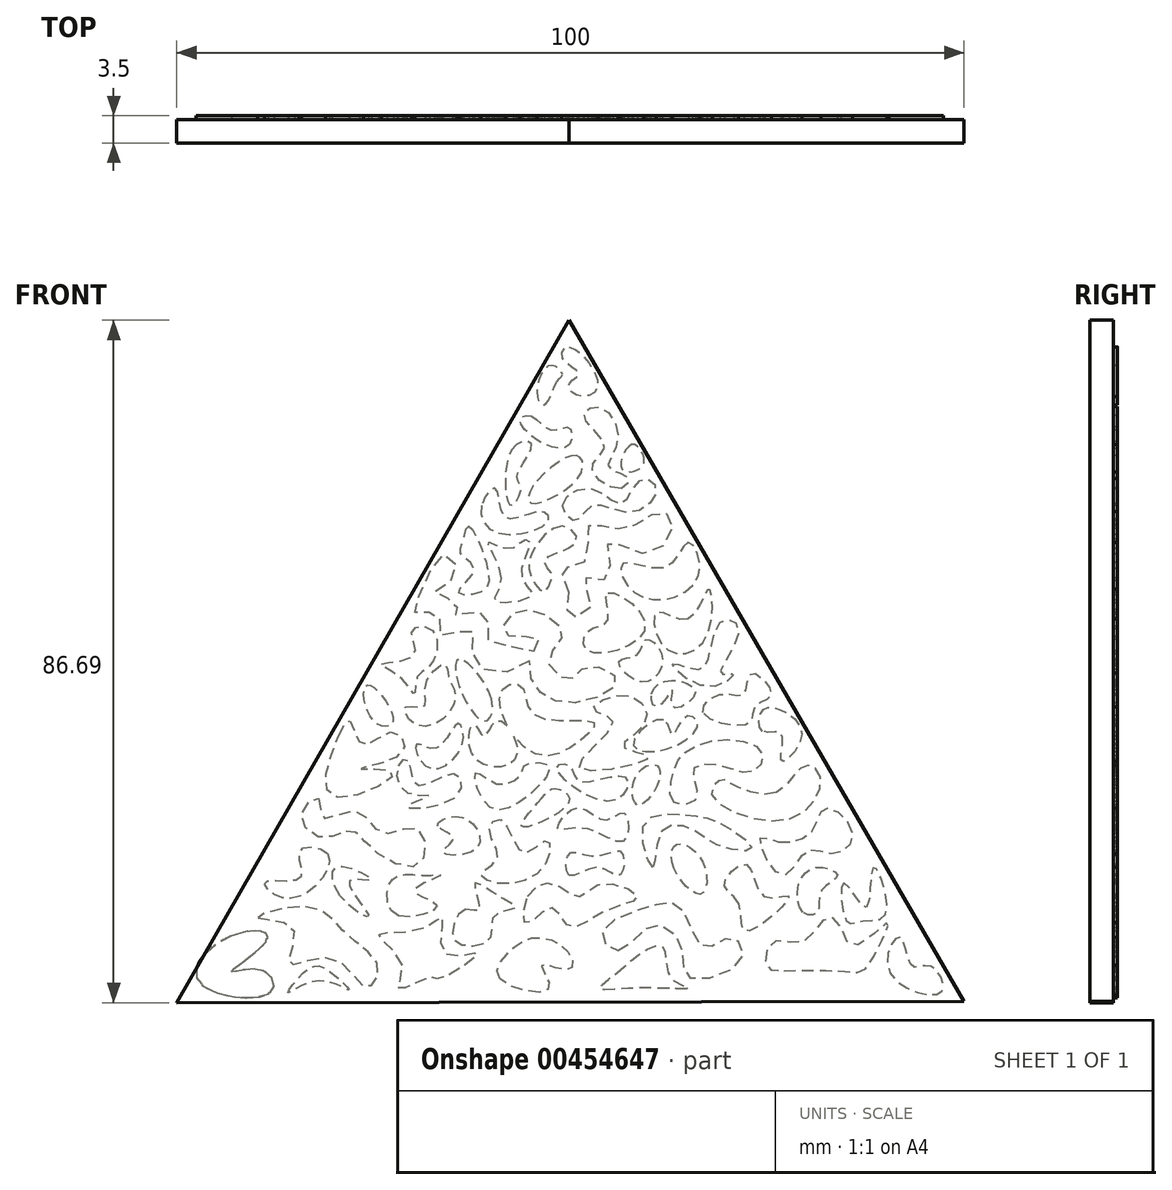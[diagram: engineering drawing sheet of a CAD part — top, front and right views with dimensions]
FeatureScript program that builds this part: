
annotation { "Feature Type Name" : "Feature", "Feature Type Description" : "" }
export const myFeature = defineFeature(function(context is Context, id is Id, definition is map)
    precondition{}
    {
        {
            var Q0;
            Q0=qCreatedBy(makeId("Front.planeOp"),FACE);
            var sketch = newSketch(context, id + "F0", { "sketchPlane" : qUnion([Q0])});
            skCircle(sketch, "E0.cCircle", {"center": v(0, 0) * mm, "radius": 28.87 * mm, "construction": true});
            skLineSegment(sketch, "E0.0", {"start": v(-49.85, 0) * mm, "end": v(0, 86.69) * mm});
            skLineSegment(sketch, "E0.1", {"start": v(0, 86.69) * mm, "end": v(50.15, 0.17) * mm});
            skLineSegment(sketch, "E0.2", {"start": v(50.15, 0.17) * mm, "end": v(-49.85, 0) * mm});
            skPoint(sketch, "E0.0.midPoint", {"position": v(25.08, -14.3) * mm});
            skSolve(sketch);
        }
        {
            var Q0;
            Q0 = qSketchRegion(id + "F0", true);
            extrude(context, id + "F1", {"entities" : qUnion([Q0]), "depth" : 3 * mm});
        }
        {
            var Q0;
            Q0=qCreatedBy(makeId("Front.planeOp"),FACE);
            var sketch = newSketch(context, id + "F2", { "sketchPlane" : qUnion([Q0])});
            skFitSpline(sketch, "E1", {"points": [v(0, 83.29) * mm, v(3.64, 78.3) * mm, v(1.1, 77.14) * mm, v(0, 78.6) * mm, v(1.2, 79.87) * mm, v(-0.86, 81.92) * mm, v(0, 83.29) * mm]});
            skFitSpline(sketch, "E2", {"points": [v(-1.54, 78.9) * mm, v(-0.86, 79.87) * mm, v(-2.42, 80.95) * mm, v(-4.08, 77.14) * mm, v(-3.1, 75.96) * mm, v(-1.54, 78.9) * mm]});
            skFitSpline(sketch, "E3", {"points": [v(-4.76, 74.5) * mm, v(-2.22, 72.74) * mm, v(0, 73.03) * mm, v(0, 70.88) * mm, v(-3.6, 71.18) * mm, v(-6.23, 74.1) * mm, v(-4.76, 74.5) * mm]});
            skFitSpline(sketch, "E4", {"points": [v(6.66, 65.32) * mm, v(2.85, 67.86) * mm, v(4.52, 70.69) * mm, v(1.88, 74.5) * mm, v(3.83, 75.67) * mm, v(6.18, 71.47) * mm, v(5, 67.95) * mm, v(7.35, 66.78) * mm, v(6.66, 65.32) * mm]});
            skFitSpline(sketch, "E5", {"points": [v(0.9, 69.52) * mm, v(-4.76, 65.32) * mm, v(-4.76, 63.46) * mm, v(1.39, 67.07) * mm, v(0.9, 69.52) * mm]});
            skFitSpline(sketch, "E6", {"points": [v(-11.11, 63.17) * mm, v(-9.06, 59.65) * mm, v(-2.62, 61.21) * mm, v(-3.6, 62.39) * mm, v(-8.09, 61.6) * mm, v(-9.36, 65.32) * mm, v(-11.11, 63.17) * mm]});
            skFitSpline(sketch, "E7", {"points": [v(-6.72, 70.88) * mm, v(-8.09, 65.32) * mm, v(-7.3, 63.17) * mm, v(-6.13, 65.32) * mm, v(-6.62, 66.98) * mm, v(-4.76, 70.88) * mm, v(-6.72, 70.88) * mm]});
            skFitSpline(sketch, "E8", {"points": [v(7.93, 70.88) * mm, v(6.66, 67.86) * mm, v(9, 67.86) * mm, v(9.4, 69.52) * mm, v(7.93, 70.88) * mm]});
            skFitSpline(sketch, "E9", {"points": [v(-0.86, 63.17) * mm, v(2.85, 65.32) * mm, v(6.66, 63.46) * mm, v(9.2, 66.49) * mm, v(11.06, 65.32) * mm, v(7.93, 62.29) * mm, v(2.85, 63.17) * mm, v(0.9, 61.21) * mm, v(-0.86, 63.17) * mm]});
            skFitSpline(sketch, "E10", {"points": [v(-0.86, 60.53) * mm, v(-4.76, 57.01) * mm, v(-4.76, 53.98) * mm, v(-3.1, 52.23) * mm, v(-2.22, 53.89) * mm, v(-2.22, 54.57) * mm, v(-3.1, 56.23) * mm, v(0.9, 58.48) * mm, v(-0.86, 60.53) * mm]});
            skFitSpline(sketch, "E11", {"points": [v(-12.77, 60.53) * mm, v(-10.33, 55.06) * mm, v(-11.11, 52.23) * mm, v(-14.04, 52.13) * mm, v(-12.1, 54.96) * mm, v(-13.75, 57.01) * mm, v(-13.46, 58.77) * mm, v(-12.77, 60.53) * mm]});
            skFitSpline(sketch, "E12", {"points": [v(-8.57, 53.89) * mm, v(-10.33, 58.48) * mm, v(-7.6, 57.7) * mm, v(-5.55, 58.87) * mm, v(-5.06, 58.28) * mm, v(-6.03, 53.98) * mm, v(-4.76, 51.74) * mm, v(-9.36, 50.96) * mm, v(-8.57, 53.89) * mm]});
            skFitSpline(sketch, "E13", {"points": [v(0, 52.13) * mm, v(-0.86, 55.06) * mm, v(2.13, 56.23) * mm, v(2.46, 60.53) * mm, v(4.43, 60.53) * mm, v(8.04, 60.53) * mm, v(11.66, 62.39) * mm, v(13.14, 60.53) * mm, v(9.69, 57.01) * mm, v(4.92, 58.44) * mm, v(4.92, 53.89) * mm, v(1.8, 53.89) * mm, v(2.79, 50.39) * mm, v(0, 49.08) * mm, v(0, 52.13) * mm]});
            skFitSpline(sketch, "E14", {"points": [v(15.1, 58.44) * mm, v(12.31, 55.32) * mm, v(6.9, 55.81) * mm, v(7.39, 53.02) * mm, v(12.15, 51.21) * mm, v(16.59, 54.83) * mm, v(15.1, 58.44) * mm]});
            skFitSpline(sketch, "E15", {"points": [v(4.92, 52.03) * mm, v(9.69, 47.76) * mm, v(2.46, 44.64) * mm, v(2.46, 47.27) * mm, v(4.92, 48.58) * mm, v(4.92, 52.03) * mm]});
            skFitSpline(sketch, "E16", {"points": [v(-7.24, 49.4) * mm, v(-3.3, 49.4) * mm, v(-0.86, 46.61) * mm, v(-2.64, 43.49) * mm, v(0, 41.03) * mm, v(2.13, 42.67) * mm, v(6.07, 41.03) * mm, v(1.64, 38.23) * mm, v(-3.62, 39.38) * mm, v(-4.94, 43.65) * mm, v(-3.95, 46.28) * mm, v(-8.06, 46.78) * mm, v(-7.24, 49.4) * mm]});
            skFitSpline(sketch, "E17", {"points": [v(-14.46, 54.17) * mm, v(-17.1, 52.03) * mm, v(-14.14, 50.72) * mm, v(-14.8, 49.4) * mm, v(-10.52, 49.4) * mm, v(-10.36, 46.12) * mm, v(-4.48, 44.68) * mm, v(-7.24, 42.18) * mm, v(-12.16, 43.65) * mm, v(-12.5, 47.43) * mm, v(-16.27, 46.61) * mm, v(-16.6, 49.4) * mm, v(-19.4, 49.4) * mm, v(-18.9, 52.03) * mm, v(-15.61, 57.01) * mm, v(-14.46, 54.17) * mm]});
            skFitSpline(sketch, "E18", {"points": [v(15.1, 48.75) * mm, v(11.16, 49.57) * mm, v(12.15, 45.13) * mm, v(17.24, 46.12) * mm, v(17.74, 52.53) * mm, v(15.1, 48.75) * mm]});
            skFitSpline(sketch, "E19", {"points": [v(-9.86, 38.56) * mm, v(-13.97, 43.65) * mm, v(-13.97, 40.2) * mm, v(-10.69, 35.77) * mm, v(-9.86, 38.56) * mm]});
            skFitSpline(sketch, "E20", {"points": [v(-8.71, 39.38) * mm, v(-6.09, 40.2) * mm, v(-4.48, 36.59) * mm, v(3.11, 35.6) * mm, v(1.8, 33.63) * mm, v(-4.48, 31.66) * mm, v(-8.71, 39.38) * mm]});
            skFitSpline(sketch, "E21", {"points": [v(1.3, 29.85) * mm, v(5.58, 35.6) * mm, v(3.11, 37.25) * mm, v(7.39, 39.05) * mm, v(9.69, 35.6) * mm, v(6.9, 32.48) * mm, v(10.18, 31.17) * mm, v(1.3, 29.85) * mm]});
            skFitSpline(sketch, "E22", {"points": [v(-25.64, 40.37) * mm, v(-22.35, 35.77) * mm, v(-24.81, 35.77) * mm, v(-25.64, 40.37) * mm]});
            skFitSpline(sketch, "E23", {"points": [v(-19.4, 32.81) * mm, v(-17.91, 29.85) * mm, v(-13.64, 32.65) * mm, v(-14.14, 35.44) * mm, v(-16.93, 32.32) * mm, v(-19.4, 32.81) * mm]});
            skFitSpline(sketch, "E24", {"points": [v(-12.1, 35.37) * mm, v(-10.83, 33.8) * mm, v(-9.07, 35.86) * mm, v(-6.72, 31.17) * mm, v(-12.1, 31.17) * mm, v(-12.1, 35.37) * mm]});
            skFitSpline(sketch, "E25", {"points": [v(6.33, 43.33) * mm, v(8.71, 44.24) * mm, v(9.7, 46.12) * mm, v(11.83, 43.9) * mm, v(9.37, 40.7) * mm, v(6.33, 43.33) * mm]});
            skFitSpline(sketch, "E26", {"points": [v(13.15, 43) * mm, v(16.02, 42.35) * mm, v(17.58, 43.41) * mm, v(19.47, 48.59) * mm, v(21.53, 47.27) * mm, v(19.23, 41.77) * mm, v(20.87, 41.85) * mm, v(17.83, 40.13) * mm, v(13.15, 43) * mm]});
            skFitSpline(sketch, "E27", {"points": [v(10.44, 39.22) * mm, v(13.15, 40.95) * mm, v(16.02, 39.22) * mm, v(13.15, 37.58) * mm, v(13.15, 39.72) * mm, v(11.18, 37.58) * mm, v(10.44, 39.22) * mm]});
            skFitSpline(sketch, "E28", {"points": [v(12, 35.94) * mm, v(8.14, 32.98) * mm, v(11.92, 32.08) * mm, v(16.35, 35.45) * mm, v(14.8, 36.35) * mm, v(13.15, 33.97) * mm, v(12, 35.94) * mm]});
            skFitSpline(sketch, "E29", {"points": [v(17, 36.84) * mm, v(19.55, 39.22) * mm, v(22.27, 39.22) * mm, v(23.17, 41.85) * mm, v(25.72, 39.22) * mm, v(23.58, 37.58) * mm, v(22.84, 35.45) * mm, v(17, 36.84) * mm]});
            skFitSpline(sketch, "E30", {"points": [v(-23.82, 43) * mm, v(-19.7, 44.15) * mm, v(-19.96, 47.27) * mm, v(-17.33, 47.27) * mm, v(-17.5, 43) * mm, v(-19.3, 41.36) * mm, v(-19.63, 39.22) * mm, v(-21.43, 41.28) * mm, v(-23.82, 43) * mm]});
            skFitSpline(sketch, "E31", {"points": [v(-20.78, 37.58) * mm, v(-18.48, 37.58) * mm, v(-18.23, 40.46) * mm, v(-15.77, 43) * mm, v(-15.27, 41.36) * mm, v(-14.46, 39.22) * mm, v(-15.93, 36.1) * mm, v(-19.7, 35.44) * mm, v(-20.78, 37.58) * mm]});
            skFitSpline(sketch, "E32", {"points": [v(-29.28, 33.9) * mm, v(-27.81, 35.77) * mm, v(-26.25, 32.81) * mm, v(-22.35, 34.39) * mm, v(-21.17, 31.85) * mm, v(-26.64, 29.7) * mm, v(-22.35, 29.21) * mm, v(-29.96, 26.18) * mm, v(-29.28, 33.9) * mm]});
            skFitSpline(sketch, "E33", {"points": [v(-21.66, 30.1) * mm, v(-20.48, 30.87) * mm, v(-19.4, 27.65) * mm, v(-14.46, 29.11) * mm, v(-14.46, 26.09) * mm, v(-20.58, 24.91) * mm, v(-17.75, 26.28) * mm, v(-20.48, 26.57) * mm, v(-21.66, 30.1) * mm]});
            skFitSpline(sketch, "E34", {"points": [v(-11.89, 29.21) * mm, v(-8.96, 27.75) * mm, v(-6.03, 29.21) * mm, v(-5.64, 30.19) * mm, v(-2.64, 30.1) * mm, v(-5.25, 26.28) * mm, v(-10.23, 24.91) * mm, v(-11.89, 29.21) * mm]});
            skFitSpline(sketch, "E35", {"points": [v(-1.55, 29.86) * mm, v(0, 30.13) * mm, v(1.29, 28.13) * mm, v(7.16, 28.61) * mm, v(5.64, 25.64) * mm, v(-1.55, 29.86) * mm]});
            skFitSpline(sketch, "E36", {"points": [v(24.57, 34.48) * mm, v(24.43, 36.97) * mm, v(26.36, 37.39) * mm, v(29.54, 34) * mm, v(26.98, 30.69) * mm, v(26.98, 34.14) * mm, v(24.57, 34.48) * mm]});
            skFitSpline(sketch, "E37", {"points": [v(8.64, 25.14) * mm, v(8.43, 28.73) * mm, v(11.06, 30.18) * mm, v(11.2, 27.63) * mm, v(8.64, 25.14) * mm]});
            skFitSpline(sketch, "E38", {"points": [v(13.3, 25.41) * mm, v(13.06, 28.55) * mm, v(14.46, 31.57) * mm, v(20.03, 33.43) * mm, v(24.56, 31.69) * mm, v(23.4, 29.36) * mm, v(19.33, 30.06) * mm, v(15.73, 29.6) * mm, v(16.2, 26) * mm, v(13.3, 25.41) * mm]});
            skFitSpline(sketch, "E39", {"points": [v(26.3, 26.7) * mm, v(20.5, 27.85) * mm, v(19.33, 28.32) * mm, v(18.06, 26.58) * mm, v(27.93, 23.32) * mm, v(31.88, 28.78) * mm, v(29.79, 30.06) * mm, v(26.3, 26.7) * mm]});
            skFitSpline(sketch, "E40", {"points": [v(-31.84, 25.95) * mm, v(-31.25, 23.5) * mm, v(-27.05, 24.39) * mm, v(-23.73, 21.55) * mm, v(-19.24, 22.14) * mm, v(-18.95, 17.65) * mm, v(-25, 19.5) * mm, v(-27.74, 21.85) * mm, v(-31.45, 20.97) * mm, v(-33.99, 24.1) * mm, v(-31.84, 25.95) * mm]});
            skFitSpline(sketch, "E41", {"points": [v(-16.7, 22.43) * mm, v(-14.94, 23.6) * mm, v(-12, 22.43) * mm, v(-11.81, 19.5) * mm, v(-16.01, 19.11) * mm, v(-14.75, 20.87) * mm, v(-16.7, 22.43) * mm]});
            skFitSpline(sketch, "E42", {"points": [v(-4, 25.36) * mm, v(-1.75, 27.22) * mm, v(0, 25.56) * mm, v(-5.95, 22.34) * mm, v(-4, 25.36) * mm]});
            skFitSpline(sketch, "E43", {"points": [v(-9.08, 18.43) * mm, v(-10.15, 22.04) * mm, v(-8.6, 23.21) * mm, v(-5.86, 19.11) * mm, v(-2.83, 20.58) * mm, v(-3.02, 17.55) * mm, v(-8.88, 15.1) * mm, v(-11.13, 16.38) * mm, v(-9.08, 18.43) * mm]});
            skFitSpline(sketch, "E44", {"points": [v(-1.46, 22.14) * mm, v(0.98, 24.78) * mm, v(4.6, 23.21) * mm, v(7.04, 24.1) * mm, v(7.04, 20.58) * mm, v(1.96, 22.14) * mm, v(-1.46, 22.14) * mm]});
            skFitSpline(sketch, "E45", {"points": [v(0, 16.18) * mm, v(0, 18.92) * mm, v(3.33, 18.62) * mm, v(6.65, 19.11) * mm, v(6.45, 16.18) * mm, v(3.62, 17.16) * mm, v(0, 16.18) * mm]});
            skFitSpline(sketch, "E46", {"points": [v(-30.72, 18.93) * mm, v(-32.46, 14.63) * mm, v(-36.87, 13.47) * mm, v(-38.61, 15.33) * mm, v(-34.08, 15.91) * mm, v(-34.2, 19.28) * mm, v(-30.72, 18.93) * mm]});
            skFitSpline(sketch, "E47", {"points": [v(-29.09, 13.59) * mm, v(-29.32, 17.3) * mm, v(-25.14, 15.56) * mm, v(-27.93, 15.45) * mm, v(-25.49, 11.03) * mm, v(-29.09, 13.59) * mm]});
            skFitSpline(sketch, "E48", {"points": [v(10.64, 17.19) * mm, v(9.48, 22.65) * mm, v(15.05, 23.81) * mm, v(19, 22.88) * mm, v(23.19, 19.63) * mm, v(19.24, 19.86) * mm, v(14.94, 22.3) * mm, v(11.57, 21.49) * mm, v(10.64, 17.19) * mm]});
            skFitSpline(sketch, "E49", {"points": [v(13.31, 17.07) * mm, v(13.66, 20.1) * mm, v(16.91, 18) * mm, v(16.8, 13.82) * mm, v(13.31, 17.07) * mm]});
            skFitSpline(sketch, "E50", {"points": [v(26.55, 20.44) * mm, v(30.97, 21.95) * mm, v(32.6, 24.74) * mm, v(35.96, 21.72) * mm, v(33.87, 18.93) * mm, v(30.16, 19.16) * mm, v(27.02, 16.18) * mm, v(24.23, 20.8) * mm, v(26.55, 20.44) * mm]});
            skFitSpline(sketch, "E51", {"points": [v(-21.65, 11.03) * mm, v(-23.05, 14.52) * mm, v(-21.54, 16.18) * mm, v(-17.94, 16.18) * mm, v(-16.31, 16.18) * mm, v(-19.68, 14.17) * mm, v(-16.78, 12.43) * mm, v(-21.65, 11.03) * mm]});
            skFitSpline(sketch, "E52", {"points": [v(-42.91, 8.48) * mm, v(-47.1, 2.67) * mm, v(-37.8, 1.4) * mm, v(-39.2, 4.18) * mm, v(-42.91, 3.95) * mm, v(-38.27, 8.24) * mm, v(-42.91, 8.48) * mm]});
            skFitSpline(sketch, "E53", {"points": [v(-39.54, 10.8) * mm, v(-35.13, 9.52) * mm, v(-35.6, 5) * mm, v(-30.13, 5.69) * mm, v(-25.72, 1.97) * mm, v(-24.2, 4.41) * mm, v(-28.28, 8.7) * mm, v(-33.04, 12.2) * mm, v(-39.54, 10.8) * mm]});
            skFitSpline(sketch, "E54", {"points": [v(-21.19, 4.76) * mm, v(-24.2, 8.6) * mm, v(-18.75, 9.4) * mm, v(-16.08, 10.8) * mm, v(-15.85, 6.27) * mm, v(-11.55, 6.27) * mm, v(-16.54, 3.02) * mm, v(-17.47, 3.25) * mm, v(-21.65, 1.74) * mm, v(-21.19, 4.76) * mm]});
            skFitSpline(sketch, "E55", {"points": [v(-13.17, 11.85) * mm, v(-14.8, 9.17) * mm, v(-13.87, 7.43) * mm, v(-10.04, 8.13) * mm, v(-9.46, 11.15) * mm, v(-6.78, 12.08) * mm, v(-8.88, 13.47) * mm, v(-12.01, 15.1) * mm, v(-11.43, 11.73) * mm, v(-13.17, 11.85) * mm]});
            skFitSpline(sketch, "E56", {"points": [v(-5.27, 13.47) * mm, v(-2.02, 15.1) * mm, v(1.23, 13.47) * mm, v(4.02, 15.1) * mm, v(8.67, 13.47) * mm, v(4.48, 11.61) * mm, v(0, 9.64) * mm, v(-2.25, 12.08) * mm, v(-5.4, 9.99) * mm, v(-5.27, 13.47) * mm]});
            skFitSpline(sketch, "E57", {"points": [v(21.56, 12.54) * mm, v(19.7, 15.1) * mm, v(22.49, 17.54) * mm, v(24.81, 13.47) * mm, v(27.95, 13.47) * mm, v(22.49, 9.06) * mm, v(21.56, 12.54) * mm]});
            skFitSpline(sketch, "E58", {"points": [v(6.23, 6.62) * mm, v(10.64, 9.87) * mm, v(14.24, 7.2) * mm, v(15.17, 3.25) * mm, v(22.02, 5.57) * mm, v(20.51, 8.24) * mm, v(17.15, 6.97) * mm, v(14.24, 11.96) * mm, v(10.18, 12.2) * mm, v(4.13, 8.83) * mm, v(6.23, 6.62) * mm]});
            skFitSpline(sketch, "E59", {"points": [v(27.25, 4.06) * mm, v(35.38, 3.95) * mm, v(37.36, 4.06) * mm, v(39.91, 8.36) * mm, v(40.5, 10.22) * mm, v(36.08, 7.2) * mm, v(34.1, 10.34) * mm, v(32.25, 10.45) * mm, v(29.58, 7.66) * mm, v(25.74, 7.66) * mm, v(25.04, 4.64) * mm, v(27.25, 4.06) * mm]});
            skFitSpline(sketch, "E60", {"points": [v(34.92, 15.21) * mm, v(35.27, 10.34) * mm, v(37, 10.34) * mm, v(40.26, 11.38) * mm, v(38.64, 17.19) * mm, v(37.7, 12.08) * mm, v(34.92, 15.21) * mm]});
            skFitSpline(sketch, "E61", {"points": [v(29.7, 11.5) * mm, v(29.34, 15.56) * mm, v(31.9, 17.19) * mm, v(34.1, 16.14) * mm, v(32.01, 14.17) * mm, v(31.55, 11.5) * mm, v(29.7, 11.5) * mm]});
            skFitSpline(sketch, "E62", {"points": [v(-35.71, 1.27) * mm, v(-33.27, 4.18) * mm, v(-30.72, 4.18) * mm, v(-27.93, 1.62) * mm, v(-31.88, 2.78) * mm, v(-35.71, 1.27) * mm]});
            skFitSpline(sketch, "E63", {"points": [v(42, 8.29) * mm, v(40.64, 4.06) * mm, v(47.28, 1.4) * mm, v(45.91, 4.64) * mm, v(43.57, 4.64) * mm, v(42, 8.29) * mm]});
            skFitSpline(sketch, "E64", {"points": [v(6.06, 3.8) * mm, v(9.18, 6.33) * mm, v(11.92, 7.11) * mm, v(12.9, 3.2) * mm, v(15.17, 1.84) * mm, v(8.01, 1.84) * mm, v(3.9, 1.84) * mm, v(6.06, 3.8) * mm]});
            skFitSpline(sketch, "E65", {"points": [v(-8.8, 3.01) * mm, v(-7.81, 6.27) * mm, v(-4.1, 8.29) * mm, v(0, 6.27) * mm, v(0, 4.18) * mm, v(-3.52, 4.77) * mm, v(-2.54, 1.84) * mm, v(-8.8, 3.01) * mm]});
            skSolve(sketch);
        }
        {
            var Q0;
            Q0 = qSketchRegion(id + "F2", true);
            extrude(context, id + "F3", {"entities" : qUnion([Q0]), "operationType" : NewBodyOperationType.ADD, "oppositeDirection" : true, "depth" : 0.5 * mm, "offsetDistance" : 25 * mm});
        }
    });
